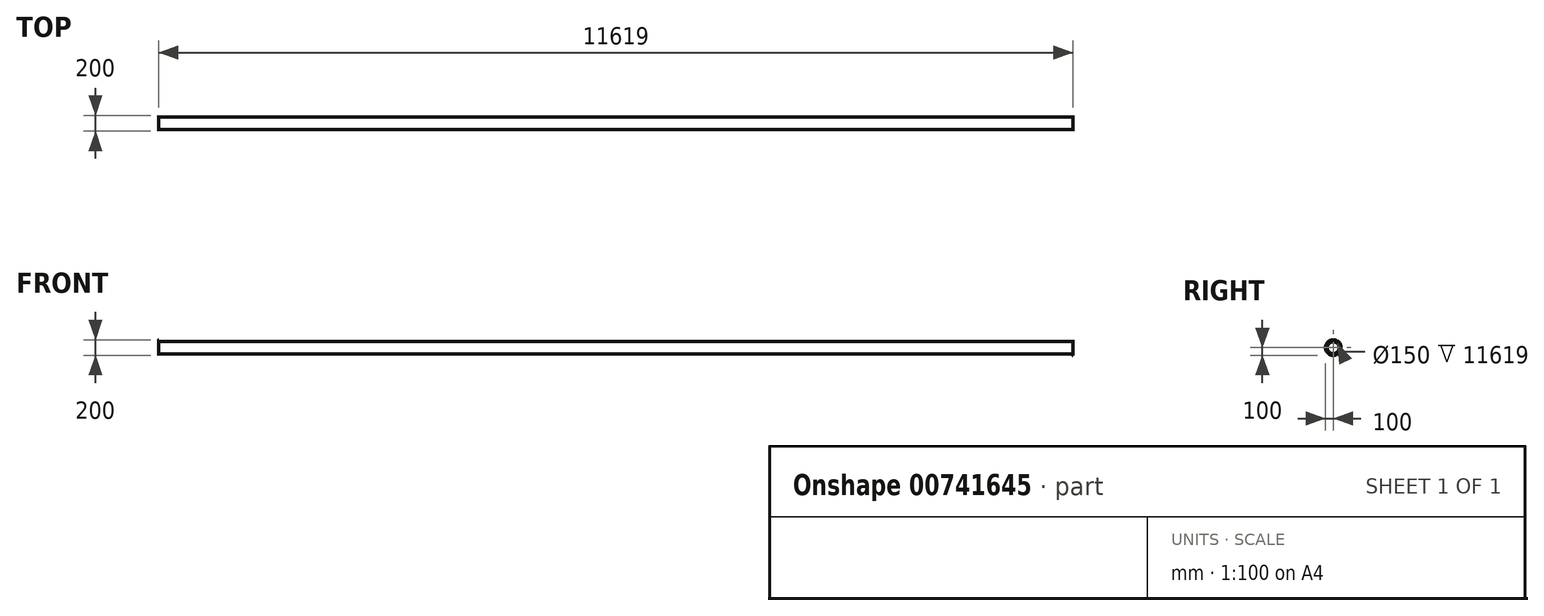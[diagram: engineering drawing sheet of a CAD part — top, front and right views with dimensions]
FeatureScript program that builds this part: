
annotation { "Feature Type Name" : "Feature", "Feature Type Description" : "" }
export const myFeature = defineFeature(function(context is Context, id is Id, definition is map)
    precondition{}
    {
        {
            var Q0;
            Q0=qCreatedBy(makeId("Front.planeOp"),FACE);
            var sketch = newSketch(context, id + "F0", { "sketchPlane" : qUnion([Q0])});
            skLineSegment(sketch, "E0", {"start": v(0, 0) * mm, "end": v(-11609, 0) * mm, "construction": true});
            skLineSegment(sketch, "E1.bottom", {"start": v(0, 75) * mm, "end": v(-11609, 75) * mm});
            skLineSegment(sketch, "E1.top", {"start": v(0, 78) * mm, "end": v(-11609, 78) * mm});
            skLineSegment(sketch, "E1.left", {"start": v(0, 75) * mm, "end": v(0, 78) * mm});
            skLineSegment(sketch, "E1.right", {"start": v(-11609, 75) * mm, "end": v(-11609, 78) * mm});
            skSolve(sketch);
        }
        {
            var Q0;
            Q0=makeQuery(id+"F0.imprint","IMPRINT",FACE,{"disambiguationData":[TD([[makeQuery(id+"F0.imprint","IMPRINT",EDGE,{"derivedFrom":sQuery(id+"F0.wireOp",EDGE,"E1.bottom")}),-1.0]])]});
            var Q1;
            Q1=sQuery(id+"F0.wireOp",EDGE,"E0");
            revolve(context, id + "F1", {"entities" : qUnion([Q0]), "axis" : qUnion([Q1]), "revolveType" : RevolveType.FULL});
        }
        {
            var Q0;
            Q0=makeQuery(id+"F1.opRevolve","SWEPT_FACE",FACE,{"disambiguationData":[OSD([sQuery(id+"F0.wireOp",EDGE,"E1.right")])]});
            var sketch = newSketch(context, id + "F2", { "sketchPlane" : qUnion([Q0])});
            skCircle(sketch, "E2", {"center": v(0, 0) * mm, "radius": 100 * mm});
            skCircle(sketch, "E3", {"center": v(0, 0) * mm, "radius": 75 * mm});
            skSolve(sketch);
        }
        {
            var Q0;
            Q0=qSketchRegion(id+"F2",true);
            extrude(context, id + "F3", {"entities" : qUnion([Q0]), "operationType" : NewBodyOperationType.ADD, "depth" : 5 * mm});
        }
        {
            var Q0;
            Q0=makeQuery(id+"F1.opRevolve","SWEPT_FACE",FACE,{"disambiguationData":[OSD([sQuery(id+"F0.wireOp",EDGE,"E1.left")])]});
            var sketch = newSketch(context, id + "F4", { "sketchPlane" : qUnion([Q0])});
            skCircle(sketch, "E4", {"center": v(0, 0) * mm, "radius": 100 * mm});
            skCircle(sketch, "E5", {"center": v(0, 0) * mm, "radius": 75 * mm});
            skSolve(sketch);
        }
        {
            var Q0;
            Q0=qSketchRegion(id+"F4",true);
            extrude(context, id + "F5", {"entities" : qUnion([Q0]), "operationType" : NewBodyOperationType.ADD, "depth" : 5 * mm});
        }
    });
